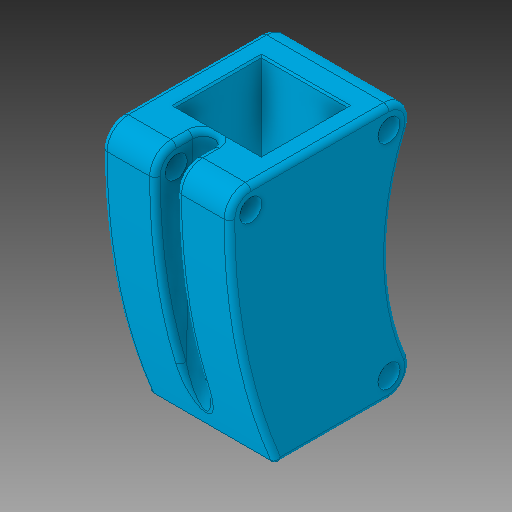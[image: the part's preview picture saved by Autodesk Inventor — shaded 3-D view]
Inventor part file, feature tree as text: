
AUTODESK INVENTOR PART (.ipt)
format: ipt  version: 2017 SP1 (Build 210196100, 196)  size: 289,792 bytes
history: native  units: in
note: dims shown in document units (in); Inventor stores cm internally (conversion verified against a paired STEP export)
features: extrude x3, fillet x3, sketch x3, chamfer x1, plane x1
ambient origin geometry x8: Origin, YZ Plane, XZ Plane, XY Plane, X Axis, Y Axis, Z Axis, Center Point
bodies: Solid1 (feature_tree)
feature tree (11):
  extrude  "Extrusion1"  Depth=3.0in TaperAngle=0.0deg
  extrude  "Extrusion2"  Depth=0.0625in
  chamfer  "Chamfer1"  Distance=0.0625in
  fillet  "Fillet1"  Radius=0.02in
  fillet  "Fillet2"  Radius=0.25in
  plane  "Work Plane2"
  extrude  "Extrusion5"  Depth=0.25in
  fillet  "Fillet4"  Radius=0.26in
  sketch  "Sketch1"  dims[d0=1.01in d3=3.0in d4=0.0in]
  sketch  "Sketch2"  dims[d9=5.0in d10=0.0in d14=0.0625in]
  sketch  "Sketch6"  dims[d16=0.25in d19=0.0625in d20=0.02in d21=0.125in d22=45.0deg d40=0.25in d45=0.25in d46=0.26in d47=0.25in d48=1.5in d49=1.125in d50=1.0in d51=0.25in d52=-0.0137in d53=0.05in d54=0.125in d55=0.5in d56=0.25in d57=0.0in d58=0.0625in d59=0.03in]
